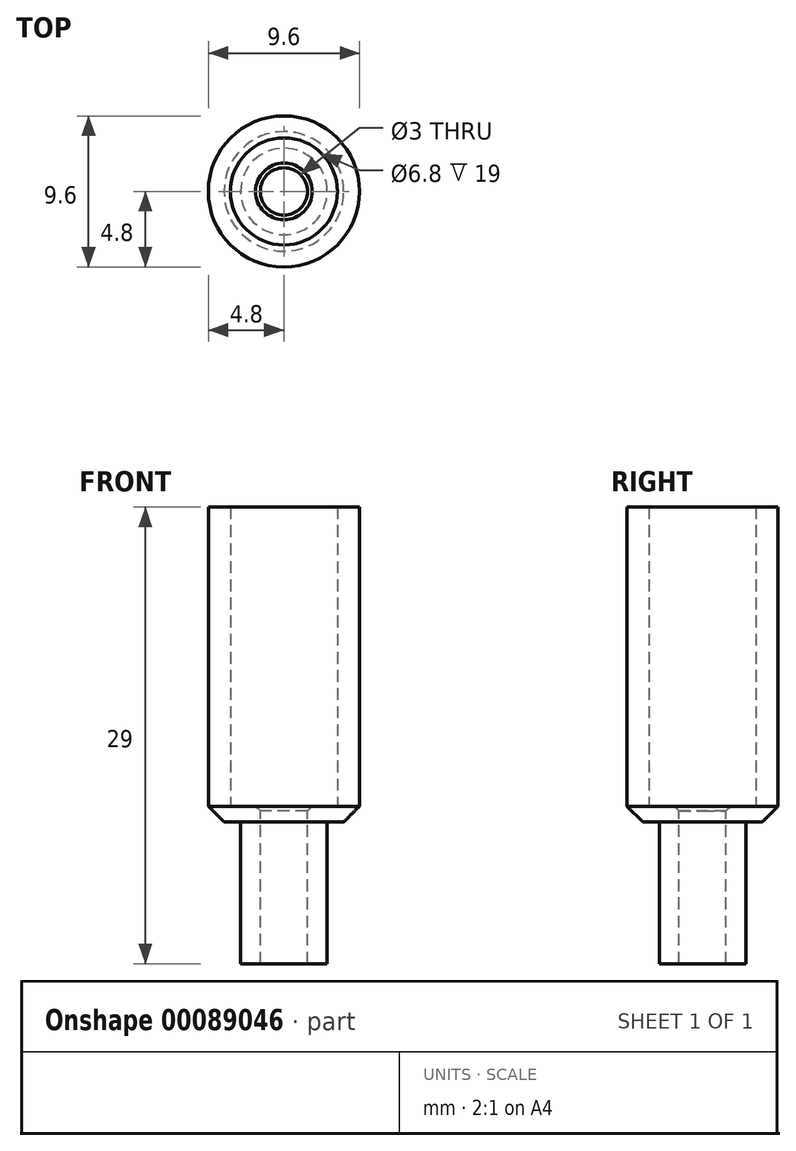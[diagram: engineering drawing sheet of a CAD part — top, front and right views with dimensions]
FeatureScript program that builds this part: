
annotation { "Feature Type Name" : "Feature", "Feature Type Description" : "" }
export const myFeature = defineFeature(function(context is Context, id is Id, definition is map)
    precondition{}
    {
        {
            var Q0;
            Q0=qCreatedBy(makeId("Top.planeOp"),FACE);
            var sketch = newSketch(context, id + "F0", { "sketchPlane" : qUnion([Q0])});
            skCircle(sketch, "E0", {"center": v(0, 0) * mm, "radius": 1.5 * mm});
            skCircle(sketch, "E1", {"center": v(0, 0) * mm, "radius": 2.75 * mm});
            skCircle(sketch, "E2", {"center": v(0, 0) * mm, "radius": 3.4 * mm});
            skCircle(sketch, "E3", {"center": v(0, 0) * mm, "radius": 4.8 * mm});
            skSolve(sketch);
        }
        {
            var Q0;
            Q0=makeQuery(id+"F0.imprint","IMPRINT",FACE,{"disambiguationData":[TD([[makeQuery(id+"F0.imprint","IMPRINT",EDGE,{"derivedFrom":sQuery(id+"F0.wireOp",EDGE,"E0")}),-1.0]])]});
            extrude(context, id + "F1", {"entities" : qUnion([Q0]), "oppositeDirection" : true, "depth" : 9 * mm});
        }
        {
            var Q0;
            Q0=makeQuery(id+"F0.imprint","IMPRINT",FACE,{"disambiguationData":[TD([[makeQuery(id+"F0.imprint","IMPRINT",EDGE,{"derivedFrom":sQuery(id+"F0.wireOp",EDGE,"E1")}),-1.0]])]});
            var Q1;
            Q1=makeQuery(id+"F0.imprint","IMPRINT",FACE,{"disambiguationData":[TD([[makeQuery(id+"F0.imprint","IMPRINT",EDGE,{"derivedFrom":sQuery(id+"F0.wireOp",EDGE,"E0")}),-1.0]])]});
            extrude(context, id + "F2", {"entities" : qUnion([Q0, Q1]), "operationType" : NewBodyOperationType.ADD, "depth" : 1 * mm});
        }
        {
            var Q0;
            Q0=makeQuery(id+"F0.imprint","IMPRINT",FACE,{"disambiguationData":[TD([[makeQuery(id+"F0.imprint","IMPRINT",EDGE,{"derivedFrom":sQuery(id+"F0.wireOp",EDGE,"E2")}),-1.0]])]});
            extrude(context, id + "F3", {"entities" : qUnion([Q0]), "operationType" : NewBodyOperationType.ADD, "depth" : 20 * mm});
        }
        {
            var Q0;
            Q0=makeQuery(id+"F3.opExtrude","CAP_EDGE",EDGE,{"disambiguationData":[OSD([sQuery(id+"F0.wireOp",EDGE,"E3")])],"isStart":true});
            chamfer(context, id + "F4", {"entities" : qUnion([Q0]), "width" : 1 * mm, "tangentPropagation" : true});
        }
        {
            var Q0;
            Q0=makeQuery(id+"F2.opExtrude","CAP_EDGE",EDGE,{"disambiguationData":[OSD([sQuery(id+"F0.wireOp",EDGE,"E0")])],"isStart":false});
            chamfer(context, id + "F5", {"entities" : qUnion([Q0]), "width" : 0.3 * mm, "tangentPropagation" : true});
        }
    });
